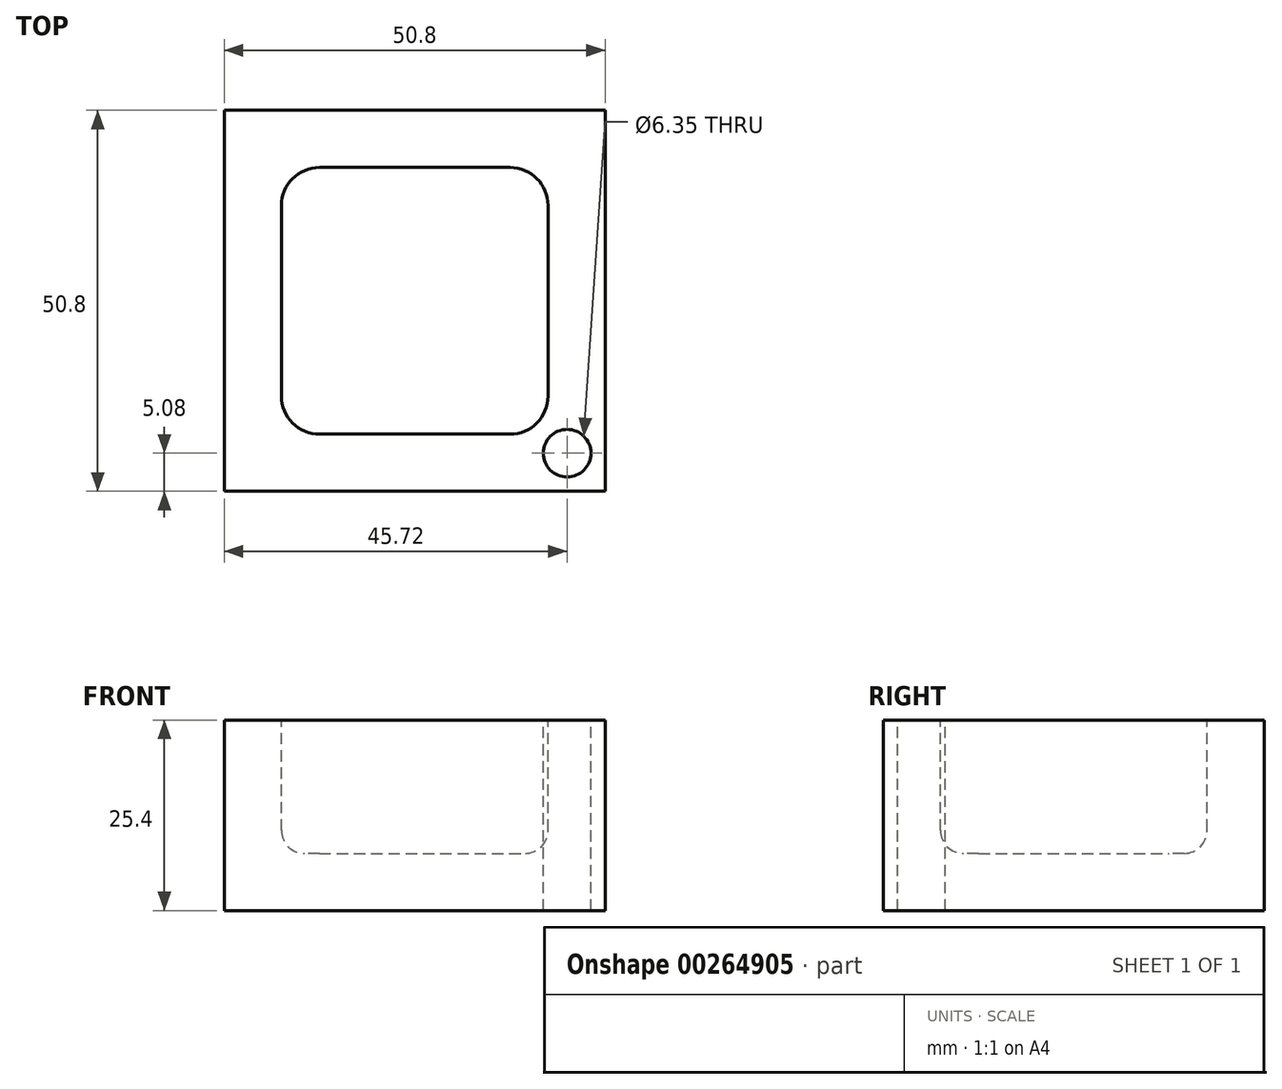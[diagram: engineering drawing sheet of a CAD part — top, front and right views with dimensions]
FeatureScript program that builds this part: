
annotation { "Feature Type Name" : "Feature", "Feature Type Description" : "" }
export const myFeature = defineFeature(function(context is Context, id is Id, definition is map)
    precondition{}
    {
        {
            var Q0;
            Q0=qCreatedBy(makeId("Front.planeOp"),FACE);
            var sketch = newSketch(context, id + "F0", { "sketchPlane" : qUnion([Q0])});
            skLineSegment(sketch, "E0.bottom", {"start": v(0, 0) * mm, "end": v(50.8, 0) * mm});
            skLineSegment(sketch, "E0.top", {"start": v(0, 25.4) * mm, "end": v(50.8, 25.4) * mm});
            skLineSegment(sketch, "E0.left", {"start": v(0, 0) * mm, "end": v(0, 25.4) * mm});
            skLineSegment(sketch, "E0.right", {"start": v(50.8, 0) * mm, "end": v(50.8, 25.4) * mm});
            skSolve(sketch);
        }
        {
            var Q0;
            Q0 = qSketchRegion(id + "F0", true);
            extrude(context, id + "F1", {"entities" : qUnion([Q0]), "depth" : 50.8 * mm});
        }
        {
            var Q0;
            Q0=makeQuery(id+"F1.opExtrude","SWEPT_FACE",FACE,{"disambiguationData":[OSD([sQuery(id+"F0.wireOp",EDGE,"E0.top")])]});
            shell(context, id + "F2", {"entities" : qUnion([Q0]), "thickness" : 7.62 * mm});
        }
        {
            var Q0;
            {var subQ0=sQuery(id+"F0.wireOp",EDGE,"E0.left");Q0=makeQuery(id+"F2.opShell","OFFSET_EDGE",EDGE,{"disambiguationData":[OSD([subQ0]),TDD([makeQuery(id+"F1.opExtrude","CAP_EDGE",EDGE,{"disambiguationData":[OSD([subQ0])],"isStart":true})])]});}
            fillet(context, id + "F3", {"entities" : qUnion([Q0]), "radius" : 5.08 * mm, "tangentPropagation" : true, "allowEdgeOverflow" : false});
        }
        {
            var Q0;
            {var subQ0=sQuery(id+"F0.wireOp",EDGE,"E0.left");Q0=makeQuery(id+"F2.opShell","OFFSET_EDGE",EDGE,{"disambiguationData":[OSD([subQ0]),TDD([makeQuery(id+"F1.opExtrude","CAP_EDGE",EDGE,{"disambiguationData":[OSD([subQ0])],"isStart":false})])]});}
            fillet(context, id + "F4", {"entities" : qUnion([Q0]), "radius" : 5.08 * mm, "tangentPropagation" : true, "allowEdgeOverflow" : false});
        }
        {
            var Q0;
            {var subQ0=sQuery(id+"F0.wireOp",EDGE,"E0.right");Q0=makeQuery(id+"F2.opShell","OFFSET_EDGE",EDGE,{"disambiguationData":[OSD([subQ0]),TDD([makeQuery(id+"F1.opExtrude","CAP_EDGE",EDGE,{"disambiguationData":[OSD([subQ0])],"isStart":false})])]});}
            fillet(context, id + "F5", {"entities" : qUnion([Q0]), "radius" : 5.08 * mm, "tangentPropagation" : true, "allowEdgeOverflow" : false});
        }
        {
            var Q0;
            {var subQ0=sQuery(id+"F0.wireOp",EDGE,"E0.right");Q0=makeQuery(id+"F2.opShell","OFFSET_EDGE",EDGE,{"disambiguationData":[OSD([subQ0]),TDD([makeQuery(id+"F1.opExtrude","CAP_EDGE",EDGE,{"disambiguationData":[OSD([subQ0])],"isStart":true})])]});}
            fillet(context, id + "F6", {"entities" : qUnion([Q0]), "radius" : 5.08 * mm, "tangentPropagation" : true, "allowEdgeOverflow" : false});
        }
        {
            var Q0;
            Q0=makeQuery(id+"F1.opExtrude","SWEPT_FACE",FACE,{"disambiguationData":[OSD([sQuery(id+"F0.wireOp",EDGE,"E0.top")])]});
            var sketch = newSketch(context, id + "F7", { "sketchPlane" : qUnion([Q0])});
            skPoint(sketch, "E1", {"position": v(45.72, -45.72) * mm});
            skPoint(sketch, "E2", {"position": v(5.08, -45.72) * mm});
            skPoint(sketch, "E3", {"position": v(5.08, -5.08) * mm});
            skPoint(sketch, "E4", {"position": v(45.72, -5.08) * mm});
            skSolve(sketch);
        }
        {
            var Q0;
            Q0=sQuery(id+"F7.wireOp",VERTEX,"E1");
            var Q1;
            Q1=makeQuery(id+"F1.opExtrude","SWEPT_BODY",BODY,{"disambiguationData":[OSD([sQuery(id+"F0.wireOp",EDGE,"E0.bottom"),sQuery(id+"F0.wireOp",EDGE,"E0.top"),sQuery(id+"F0.wireOp",EDGE,"E0.left"),sQuery(id+"F0.wireOp",EDGE,"E0.right")])]});
            hole(context, id + "F8", {"style" : HoleStyle.SIMPLE, "endStyle" : HoleEndStyle.THROUGH, "holeDiameter" : 6.35 * mm, "tappedDepth" : 12.7 * mm, "tapClearance" : 3, "locations" : qUnion([Q0]), "scope" : qUnion([Q1])});
        }
        {
            var Q0;
            {var subQ0=sQuery(id+"F0.wireOp",EDGE,"E0.bottom");Q0=makeQuery(id+"F2.opShell","OFFSET_EDGE",EDGE,{"disambiguationData":[OSD([subQ0]),TDD([makeQuery(id+"F1.opExtrude","CAP_EDGE",EDGE,{"disambiguationData":[OSD([subQ0])],"isStart":true})])]});}
            fillet(context, id + "F9", {"entities" : qUnion([Q0]), "radius" : 3.07 * mm, "tangentPropagation" : true, "allowEdgeOverflow" : false});
        }
    });
